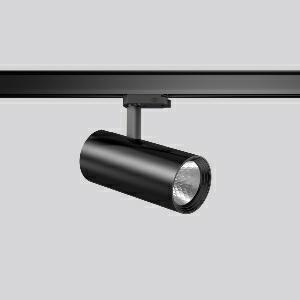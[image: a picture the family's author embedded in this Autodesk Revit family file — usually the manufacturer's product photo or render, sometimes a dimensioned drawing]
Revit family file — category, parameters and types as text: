
# Revit family: deecos_s_mini_742196_003_2_94b0
name_source: partatom
category: Lighting Fixtures
units: mm (PartAtom-declared; Revit-internal decimal feet)

## family parameters
Cut with Voids When Loaded = No
Host = Face
Light Source = No
Part Type = Normal
Room Calculation Point = No
Round Connector Dimension = Use Diameter
Shared = No

## types (1)
- DEECOS S mini (1 x LED Modul 927, 2300 lm, 2700)
    Apparent Load = 20 VA
    Approval mark = CE
    CIE Flux Codes = 99 100 100 100 100
    Color Rendering = 92
    Color Temperature = 2700
    Default Elevation = 1800 mm
    Description = Series: DEECOS S mini
LED surface-mounted projector in modern design with no visible cooling ribs. Housing: die-cast aluminium, powder-coated. Rotation range: 356°. Swivel range: 90°. Black plastic ring and recessed LED to prevent glare from the side. Optical assembly with reflector made of MIRO-Silver with 98% total light reflection for outstanding efficiency - can be changed without tools. Best colour rendering index Ra>90. With multi adaptor for 3-circuit tracks 230 V. Suitable for Track on ceiling, Wall track. High quality converter without flickering and stroboscopic effect. The following accessories can be mounted without use of tools: interchangeable lenses, decorative glasses, honeycomb louvre, clear and frosted diffusers, white interchangeable plastic ring. 
Colour: deep black, matt (RAL 9005)
Diameter: 87 mm
Height: 214 mm
Lamp: LED
Socket: without socket
Colour temperature: 2700K
Colour rendering index (CRI): 92
System power: 20 W
Rated luminous flux: 2300 lm
Luminous efficiency: 115 lm/W
Control gear: Regulated power supply
Protection class: I
Type of protection: IP 20
    Height = 214 mm
    Lamp = 1 x LED Modul 927
    Lamp Light Flux = 2300 lm
    Lamp count = 1
    Length = 87 mm
    Lifetime = 50000 h
    Luminous efficacy = 115 lm/W
    Manufacturer = RZB
    ModVariant = No
    Model = 742196.003.2
    Mounting Place = Ceiling
    Mounting Type = Rail mounted
    Number of Poles = 1
    OnlyDefault = Yes
    Power Factor = 1
    Product Name = DEECOS S mini
    Product group = Track mounted projectors
    ProductGroupID = 301
    Protection Class = Protection class I
    Protection Degree = IP 20
    RLX_Detail_Level = 1
    RLX_Emergency_Light_Flux = 0 lm
    RLX_Emergency_Type = 0
    RLX_Emergency_Type_DB = No
    RlxData = <blob elided: 38689 chars, md5=ea1f08c5>
    Socket = socket
    Standby Power = 0 W
    System Light Flux = 2300 lm
    System Power = 20 W
    Type Comments = Product without accessories
    Type Image = 741926.003.jpg
    URL = http://relux.com
    VarID = ---
    Voltage = 230 V
    Voltage Range = 220-240 V
    Weight = 0.00 kg
    Width = 0 mm  [stored 0 ft]

note: [stored X ft] marks values corroborated as IEEE doubles in the binary element streams (Revit-internal decimal feet)

## geometry (parser evidence)
native form markers: Blend x4, Sweep x11
no freeform markers — native parametric forms only
